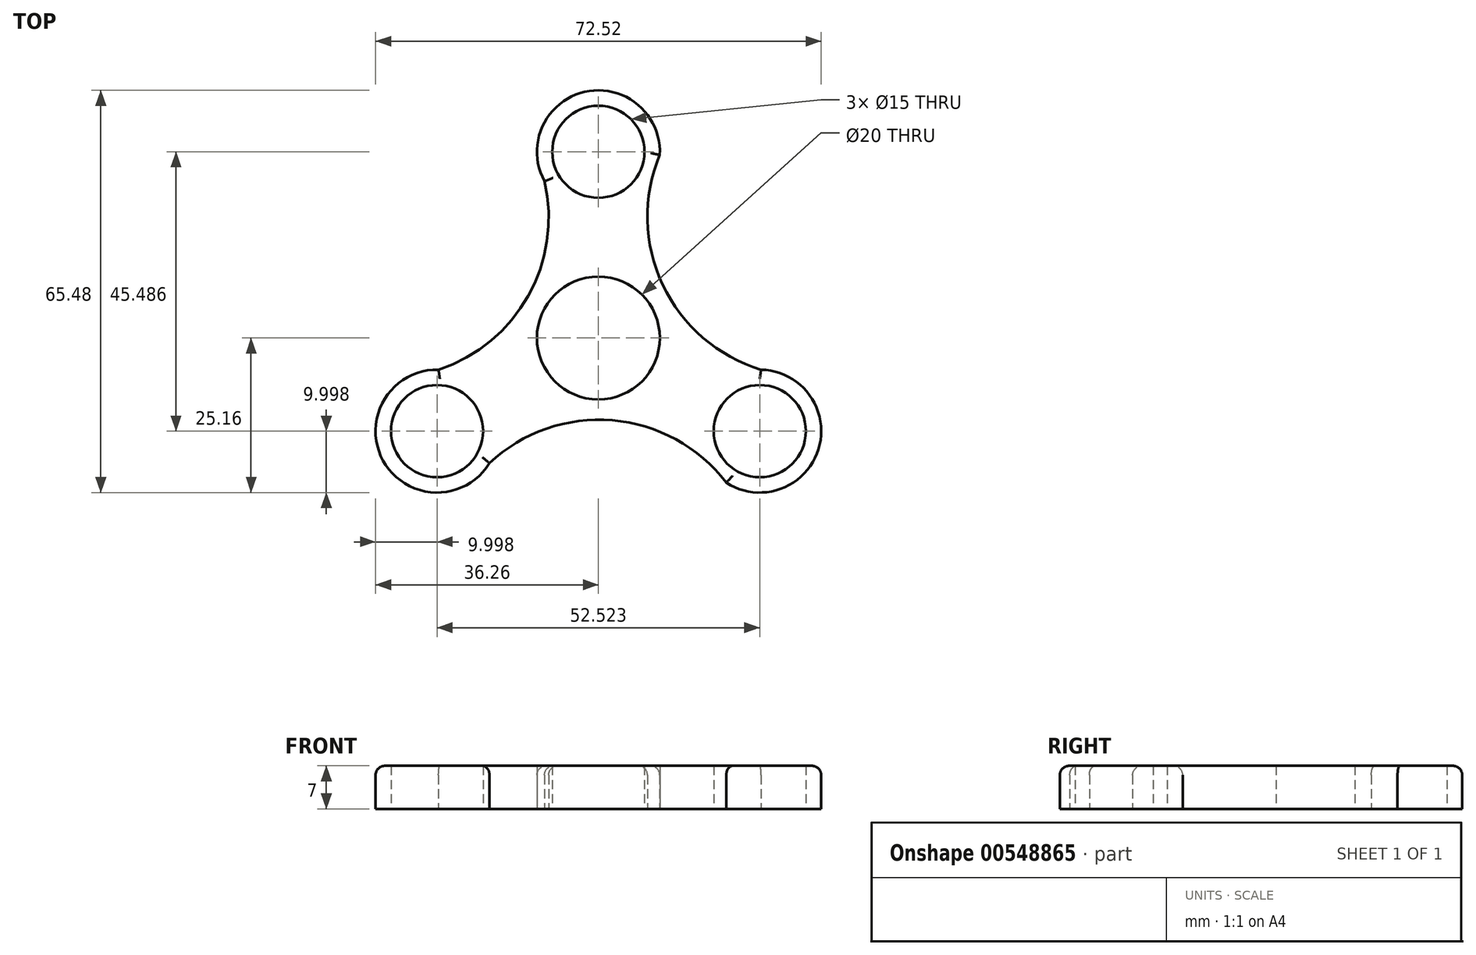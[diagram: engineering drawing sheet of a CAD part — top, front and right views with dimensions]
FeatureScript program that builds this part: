
annotation { "Feature Type Name" : "Feature", "Feature Type Description" : "" }
export const myFeature = defineFeature(function(context is Context, id is Id, definition is map)
    precondition{}
    {
        {
            var Q0;
            Q0=qCreatedBy(makeId("Top.planeOp"),FACE);
            var sketch = newSketch(context, id + "F0", { "sketchPlane" : qUnion([Q0])});
            skCircle(sketch, "E0", {"center": v(0, 0) * mm, "radius": 10 * mm});
            skArc(sketch, "E1", {"start": v(9.99, 29.8) * mm, "mid": v(-2.22, 40.07) * mm, "end": v(-8.77, 25.52) * mm});
            skArc(sketch, "E2.1.0", {"start": v(-26.02, -5.17) * mm, "mid": v(-35.04, -19.96) * mm, "end": v(-17.72, -20.36) * mm});
            skArc(sketch, "E2.2.0", {"start": v(20.82, -23.55) * mm, "mid": v(35.82, -18.11) * mm, "end": v(26.49, -5.16) * mm});
            skArc(sketch, "E3", {"start": v(9.99, 29.8) * mm, "mid": v(10.48, 8.66) * mm, "end": v(26.49, -5.16) * mm});
            skArc(sketch, "E4.1.0", {"start": v(-26.02, -5.17) * mm, "mid": v(-11.43, 6.83) * mm, "end": v(-8.77, 25.52) * mm});
            skArc(sketch, "E4.2.0", {"start": v(20.82, -23.55) * mm, "mid": v(2.26, -13.4) * mm, "end": v(-17.72, -20.36) * mm});
            skCircle(sketch, "E5", {"center": v(-26.26, -15.16) * mm, "radius": 7.5 * mm});
            skCircle(sketch, "E6", {"center": v(26.26, -15.16) * mm, "radius": 7.5 * mm});
            skCircle(sketch, "E7", {"center": v(0, 30.32) * mm, "radius": 7.5 * mm});
            skPoint(sketch, "E8.orphan", {"position": v(-30.8, -6.25) * mm});
            skSolve(sketch);
        }
        {
            var Q0;
            Q0=makeQuery(id+"F0.imprint","IMPRINT",FACE,{"disambiguationData":[TD([[makeQuery(id+"F0.imprint","IMPRINT",EDGE,{"derivedFrom":sQuery(id+"F0.wireOp",EDGE,"E0")}),-1.0]])]});
            extrude(context, id + "F1", {"entities" : qUnion([Q0]), "depth" : 7 * mm, "offsetDistance" : 25 * mm});
        }
        {
            var Q0;
            Q0=makeQuery(id+"F1.opExtrude","CAP_EDGE",EDGE,{"disambiguationData":[OSD([sQuery(id+"F0.wireOp",EDGE,"E3")])],"isStart":false});
            var Q1;
            Q1=makeQuery(id+"F1.opExtrude","CAP_EDGE",EDGE,{"disambiguationData":[OSD([sQuery(id+"F0.wireOp",EDGE,"E4.1.0")])],"isStart":false});
            var Q2;
            Q2=makeQuery(id+"F1.opExtrude","CAP_EDGE",EDGE,{"disambiguationData":[OSD([sQuery(id+"F0.wireOp",EDGE,"E4.2.0")])],"isStart":false});
            var Q3;
            Q3=makeQuery(id+"F1.opExtrude","CAP_EDGE",EDGE,{"disambiguationData":[OSD([sQuery(id+"F0.wireOp",EDGE,"E2.2.0")])],"isStart":false});
            var Q4;
            Q4=makeQuery(id+"F1.opExtrude","CAP_EDGE",EDGE,{"disambiguationData":[OSD([sQuery(id+"F0.wireOp",EDGE,"E2.1.0")])],"isStart":false});
            var Q5;
            Q5=makeQuery(id+"F1.opExtrude","CAP_EDGE",EDGE,{"disambiguationData":[OSD([sQuery(id+"F0.wireOp",EDGE,"E1")])],"isStart":false});
            fillet(context, id + "F2", {"entities" : qUnion([Q0, Q1, Q2, Q3, Q4, Q5]), "radius" : 1.5 * mm, "tangentPropagation" : true, "allowEdgeOverflow" : false});
        }
    });
